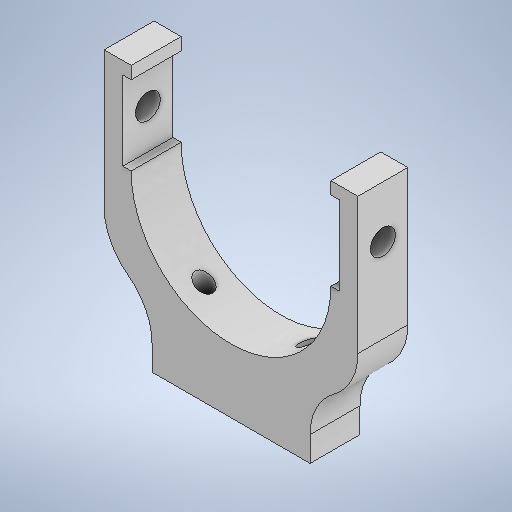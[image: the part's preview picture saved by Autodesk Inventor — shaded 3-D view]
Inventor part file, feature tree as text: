
AUTODESK INVENTOR PART (.ipt)
format: ipt  version: 2025.1 (Build 291241000, 241)  size: 315,392 bytes
history: native  units: mm
features: sketch x4, hole x3, extrude x1
ambient origin geometry x8: Origin, YZ Plane, XZ Plane, XY Plane, X Axis, Y Axis, Z Axis, Center Point
bodies: Volumenkörper1 (feature_tree)
feature tree (8):
  extrude  "Extrusion1"  Depth=19.0mm
  hole  "Bohrung1"  [1 undecoded]
  hole  "Bohrung2"  [1 undecoded]
  hole  "Bohrung3"  [1 undecoded]
  sketch  "Skizze1"  dims[d2=2.0mm d3=19.0mm]
  sketch  "Skizze2"  dims[d4=14.0mm d5=14.0mm]
  sketch  "Skizze3"  dims[d6=38.0mm d10=19.0mm]
  sketch  "Skizze4"  dims[d12=2.0mm d13=24.0mm d14=24.0mm d18=4.5mm d19=4.5mm d20=24.0mm d26=12.0mm d27=0.0mm d28=4.134mm d29=10.0mm d30=4.0mm d31=2.0mm d32=90.0deg d33=8.0mm d34=0.0mm d35=25.0mm d36=12.5mm d37=6.0mm d38=10.0mm d39=4.0mm d40=2.0mm d41=90.0deg d42=8.0mm d43=0.0mm d44=12.5mm d46=6.0mm d47=6.0mm d48=4.0mm d49=2.0mm d50=90.0deg d51=8.0mm d52=0.0mm d53=12.5mm d54=19.0mm d55=6.0mm d56=14.0mm d57=14.0mm d58=42.871892mm d59=10.75mm]
note: 3 required parameter values undecoded (feature->parameter linkage not recoverable at this tier; creation-order binding heuristic only, values carry confidence <= 0.55)
